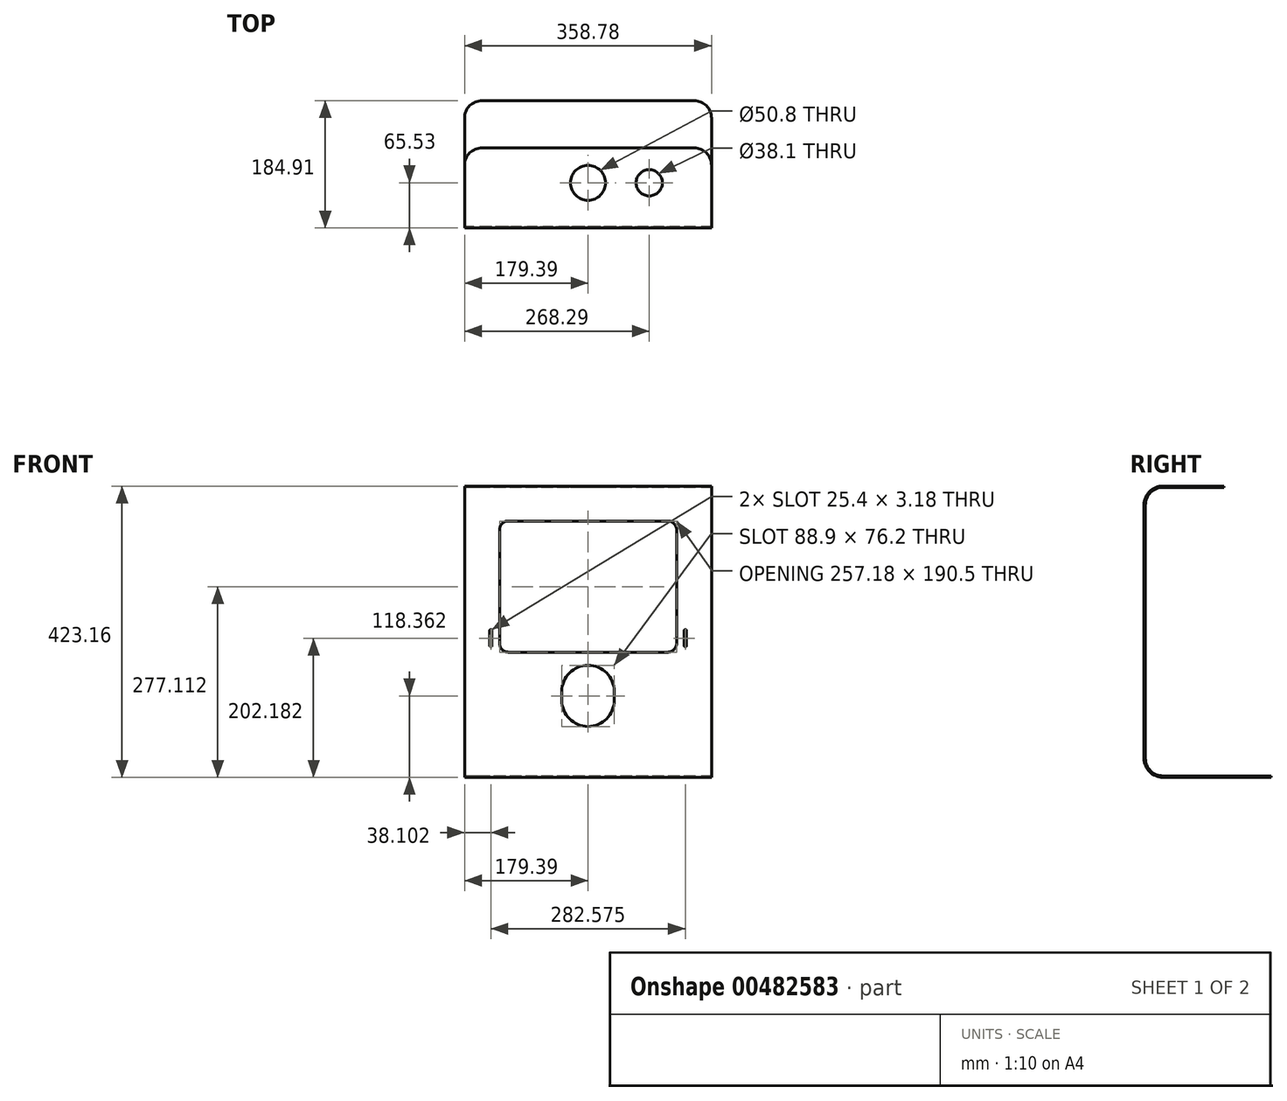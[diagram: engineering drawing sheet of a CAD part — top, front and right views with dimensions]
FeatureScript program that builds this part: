
annotation { "Feature Type Name" : "Feature", "Feature Type Description" : "" }
export const myFeature = defineFeature(function(context is Context, id is Id, definition is map)
    precondition{}
    {
        {
            var Q0;
            Q0=qCreatedBy(makeId("Right.planeOp"),FACE);
            var sketch = newSketch(context, id + "F0", { "sketchPlane" : qUnion([Q0])});
            skLineSegment(sketch, "E0", {"start": v(0, 184.15) * mm, "end": v(0, -184.15) * mm});
            skLineSegment(sketch, "E1", {"start": v(25.4, -209.55) * mm, "end": v(182.88, -209.55) * mm});
            skLineSegment(sketch, "E2", {"start": v(25.4, 209.55) * mm, "end": v(114.3, 209.55) * mm});
            skPoint(sketch, "E3.visualSharp", {"position": v(0, 209.55) * mm});
            skArc(sketch, "E3.filletArc", {"start": v(25.4, 209.55) * mm, "mid": v(7.44, 202.11) * mm, "end": v(0, 184.15) * mm});
            skPoint(sketch, "E4.visualSharp", {"position": v(0, -209.55) * mm});
            skArc(sketch, "E4.filletArc", {"start": v(0, -184.15) * mm, "mid": v(7.44, -202.11) * mm, "end": v(25.4, -209.55) * mm});
            skLineSegment(sketch, "E5.0", {"start": v(25.4, 211.58) * mm, "end": v(114.3, 211.58) * mm});
            skLineSegment(sketch, "E5.1", {"start": v(25.4, -211.58) * mm, "end": v(182.88, -211.58) * mm});
            skArc(sketch, "E5.2", {"start": v(-2.03, -184.15) * mm, "mid": v(6, -203.55) * mm, "end": v(25.4, -211.58) * mm});
            skLineSegment(sketch, "E5.3", {"start": v(-2.03, 184.15) * mm, "end": v(-2.03, -184.15) * mm});
            skArc(sketch, "E5.4", {"start": v(25.4, 211.58) * mm, "mid": v(6, 203.55) * mm, "end": v(-2.03, 184.15) * mm});
            skLineSegment(sketch, "E6", {"start": v(114.3, 211.58) * mm, "end": v(114.3, 209.55) * mm});
            skLineSegment(sketch, "E7", {"start": v(182.88, -209.55) * mm, "end": v(182.88, -211.58) * mm});
            skSolve(sketch);
        }
        {
            var Q0;
            Q0=qSketchRegion(id+"F0",true);
            extrude(context, id + "F1", {"entities" : qUnion([Q0]), "endBound" : BoundingType.SYMMETRIC, "depth" : 358.77 * mm});
        }
        {
            var Q0;
            Q0=makeQuery(id+"F1.opExtrude","CAP_EDGE",EDGE,{"disambiguationData":[OSD([sQuery(id+"F0.wireOp",EDGE,"E6")])],"isStart":false});
            var Q1;
            Q1=makeQuery(id+"F1.opExtrude","CAP_EDGE",EDGE,{"disambiguationData":[OSD([sQuery(id+"F0.wireOp",EDGE,"E6")])],"isStart":true});
            var Q2;
            Q2=makeQuery(id+"F1.opExtrude","CAP_EDGE",EDGE,{"disambiguationData":[OSD([sQuery(id+"F0.wireOp",EDGE,"E7")])],"isStart":true});
            var Q3;
            Q3=makeQuery(id+"F1.opExtrude","CAP_EDGE",EDGE,{"disambiguationData":[OSD([sQuery(id+"F0.wireOp",EDGE,"E7")])],"isStart":false});
            fillet(context, id + "F2", {"entities" : qUnion([Q0, Q1, Q2, Q3]), "radius" : 25.4 * mm, "tangentPropagation" : true, "allowEdgeOverflow" : false});
        }
        {
            var Q0;
            Q0=makeQuery(id+"F1.opExtrude","SWEPT_FACE",FACE,{"disambiguationData":[OSD([sQuery(id+"F0.wireOp",EDGE,"E5.3")])]});
            var sketch = newSketch(context, id + "F3", { "sketchPlane" : qUnion([Q0])});
            skLineSegment(sketch, "E8.bottom", {"start": v(-115.89, 160.78) * mm, "end": v(115.89, 160.78) * mm});
            skLineSegment(sketch, "E8.top", {"start": v(-115.89, -29.72) * mm, "end": v(115.89, -29.72) * mm});
            skLineSegment(sketch, "E8.left", {"start": v(-128.59, 148.08) * mm, "end": v(-128.59, -17.02) * mm});
            skLineSegment(sketch, "E8.right", {"start": v(128.59, 148.08) * mm, "end": v(128.59, -17.02) * mm});
            skPoint(sketch, "E9.visualSharp", {"position": v(-128.59, 160.78) * mm});
            skArc(sketch, "E9.filletArc", {"start": v(-115.89, 160.78) * mm, "mid": v(-124.87, 157.06) * mm, "end": v(-128.59, 148.08) * mm});
            skPoint(sketch, "E10.visualSharp", {"position": v(128.59, 160.78) * mm});
            skArc(sketch, "E10.filletArc", {"start": v(128.59, 148.08) * mm, "mid": v(124.87, 157.06) * mm, "end": v(115.89, 160.78) * mm});
            skPoint(sketch, "E11.visualSharp", {"position": v(128.59, -29.72) * mm});
            skArc(sketch, "E11.filletArc", {"start": v(115.89, -29.72) * mm, "mid": v(124.87, -26) * mm, "end": v(128.59, -17.02) * mm});
            skPoint(sketch, "E12.visualSharp", {"position": v(-128.59, -29.72) * mm});
            skArc(sketch, "E12.filletArc", {"start": v(-128.59, -17.02) * mm, "mid": v(-124.87, -26) * mm, "end": v(-115.89, -29.72) * mm});
            skSolve(sketch);
        }
        {
            var Q0;
            Q0=qSketchRegion(id+"F3",true);
            extrude(context, id + "F4", {"entities" : qUnion([Q0]), "operationType" : NewBodyOperationType.REMOVE, "oppositeDirection" : true, "depth" : 2.03 * mm});
        }
        {
            var Q0;
            Q0=makeQuery(id+"F1.opExtrude","SWEPT_FACE",FACE,{"disambiguationData":[OSD([sQuery(id+"F0.wireOp",EDGE,"E5.3")])]});
            var sketch = newSketch(context, id + "F5", { "sketchPlane" : qUnion([Q0])});
            skArc(sketch, "E13", {"start": v(38.1, -86.87) * mm, "mid": v(0, -48.77) * mm, "end": v(-38.1, -86.87) * mm});
            skArc(sketch, "E14", {"start": v(-38.1, -99.57) * mm, "mid": v(0, -137.67) * mm, "end": v(38.1, -99.57) * mm});
            skLineSegment(sketch, "E15", {"start": v(-38.1, -86.87) * mm, "end": v(-38.1, -99.57) * mm});
            skLineSegment(sketch, "E16", {"start": v(38.1, -86.87) * mm, "end": v(38.1, -99.57) * mm});
            skSolve(sketch);
        }
        {
            var Q0;
            Q0=qSketchRegion(id+"F5",true);
            extrude(context, id + "F6", {"entities" : qUnion([Q0]), "operationType" : NewBodyOperationType.REMOVE, "oppositeDirection" : true, "depth" : 2.03 * mm});
        }
        {
            var Q0;
            Q0=makeQuery(id+"F1.opExtrude","SWEPT_FACE",FACE,{"disambiguationData":[OSD([sQuery(id+"F0.wireOp",EDGE,"E5.3")])]});
            var sketch = newSketch(context, id + "F7", { "sketchPlane" : qUnion([Q0])});
            skLineSegment(sketch, "E17.left", {"start": v(139.7, 1.71) * mm, "end": v(139.7, -20.51) * mm});
            skLineSegment(sketch, "E17.right", {"start": v(142.87, 1.71) * mm, "end": v(142.87, -20.51) * mm});
            skArc(sketch, "E18", {"start": v(142.87, 1.71) * mm, "mid": v(141.29, 3.3) * mm, "end": v(139.7, 1.71) * mm});
            skArc(sketch, "E19", {"start": v(139.7, -20.51) * mm, "mid": v(141.29, -22.1) * mm, "end": v(142.87, -20.51) * mm});
            skLineSegment(sketch, "E20.left", {"start": v(-142.88, 1.71) * mm, "end": v(-142.88, -20.51) * mm});
            skLineSegment(sketch, "E20.right", {"start": v(-139.7, 1.71) * mm, "end": v(-139.7, -20.51) * mm});
            skArc(sketch, "E21", {"start": v(-139.7, 1.71) * mm, "mid": v(-141.29, 3.3) * mm, "end": v(-142.87, 1.71) * mm});
            skArc(sketch, "E22", {"start": v(-142.87, -20.51) * mm, "mid": v(-141.29, -22.1) * mm, "end": v(-139.7, -20.51) * mm});
            skSolve(sketch);
        }
        {
            var Q0;
            Q0=makeQuery(id+"F7.imprint","IMPRINT",FACE,{"disambiguationData":[TD([[makeQuery(id+"F7.imprint","IMPRINT",EDGE,{"derivedFrom":sQuery(id+"F7.wireOp",EDGE,"E17.left")}),1.0]])]});
            var Q1;
            Q1=makeQuery(id+"F7.imprint","IMPRINT",FACE,{"disambiguationData":[TD([[makeQuery(id+"F7.imprint","IMPRINT",EDGE,{"derivedFrom":sQuery(id+"F7.wireOp",EDGE,"E20.left")}),1.0]])]});
            extrude(context, id + "F8", {"entities" : qUnion([Q0, Q1]), "operationType" : NewBodyOperationType.REMOVE, "oppositeDirection" : true, "depth" : 2.54 * mm});
        }
        {
            var Q0;
            Q0=makeQuery(id+"F1.opExtrude","SWEPT_FACE",FACE,{"disambiguationData":[OSD([sQuery(id+"F0.wireOp",EDGE,"E5.0")])]});
            var sketch = newSketch(context, id + "F9", { "sketchPlane" : qUnion([Q0])});
            skCircle(sketch, "E23", {"center": v(0, 63.5) * mm, "radius": 25.4 * mm});
            skSolve(sketch);
        }
        {
            var Q0;
            Q0=qSketchRegion(id+"F9",true);
            extrude(context, id + "F10", {"entities" : qUnion([Q0]), "operationType" : NewBodyOperationType.REMOVE, "oppositeDirection" : true, "depth" : 25.4 * mm});
        }
        {
            var Q0;
            Q0=makeQuery(id+"F1.opExtrude","SWEPT_FACE",FACE,{"disambiguationData":[OSD([sQuery(id+"F0.wireOp",EDGE,"E5.0")])]});
            var sketch = newSketch(context, id + "F11", { "sketchPlane" : qUnion([Q0])});
            skCircle(sketch, "E24", {"center": v(88.9, 63.5) * mm, "radius": 19.05 * mm});
            skSolve(sketch);
        }
        {
            var Q0;
            Q0=qSketchRegion(id+"F11",true);
            extrude(context, id + "F12", {"entities" : qUnion([Q0]), "operationType" : NewBodyOperationType.REMOVE, "oppositeDirection" : true, "depth" : 25.4 * mm});
        }
    });
